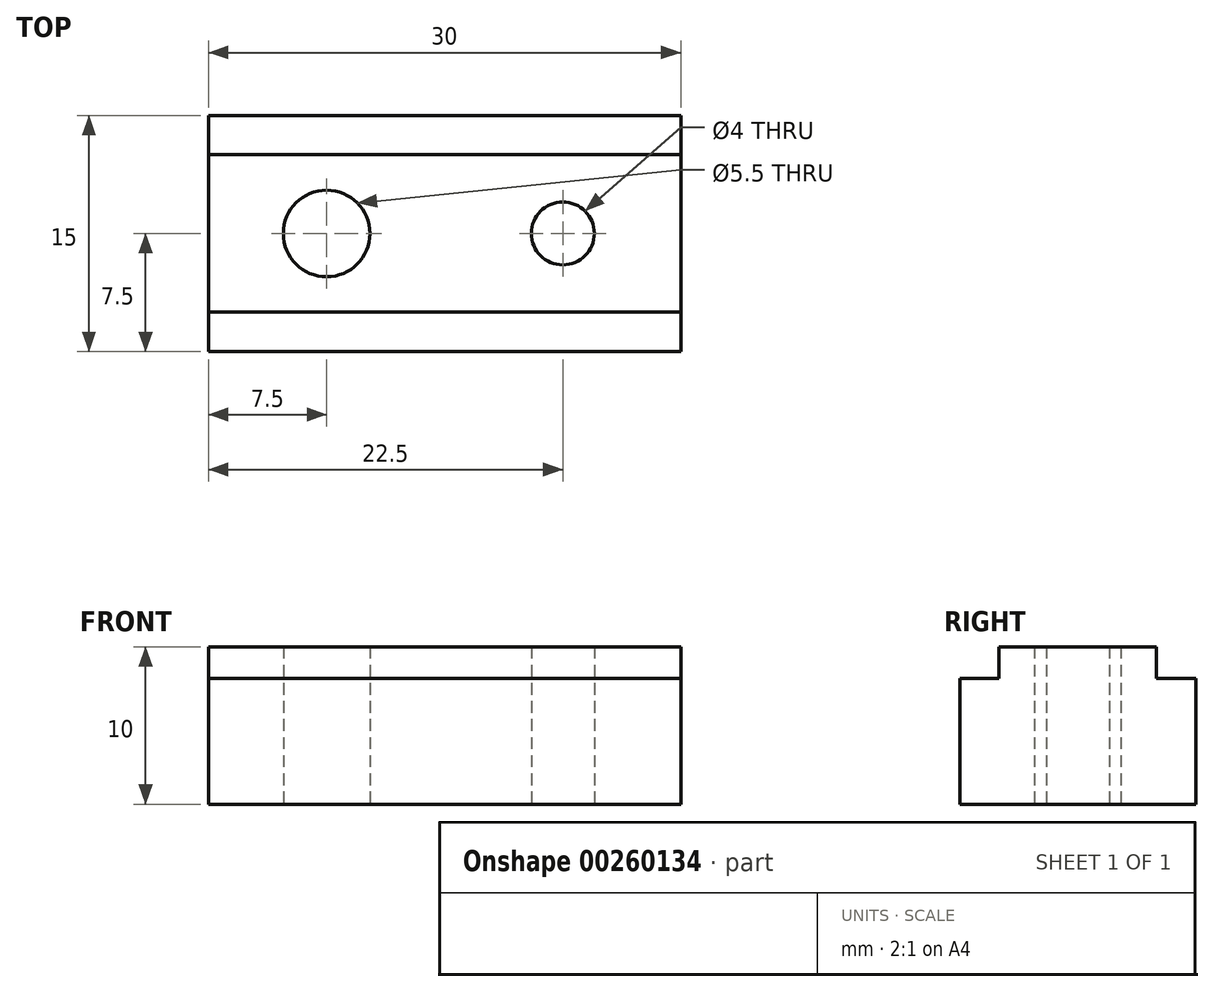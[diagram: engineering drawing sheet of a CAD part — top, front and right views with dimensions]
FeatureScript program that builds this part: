
annotation { "Feature Type Name" : "Feature", "Feature Type Description" : "" }
export const myFeature = defineFeature(function(context is Context, id is Id, definition is map)
    precondition{}
    {
        {
            var Q0;
            Q0=qCreatedBy(makeId("Top.planeOp"),FACE);
            var sketch = newSketch(context, id + "F0", { "sketchPlane" : qUnion([Q0])});
            skLineSegment(sketch, "E0.bottom", {"start": v(-15, -7.5) * mm, "end": v(15, -7.5) * mm});
            skLineSegment(sketch, "E0.top", {"start": v(-15, 7.5) * mm, "end": v(15, 7.5) * mm});
            skLineSegment(sketch, "E0.left", {"start": v(-15, -7.5) * mm, "end": v(-15, 7.5) * mm});
            skLineSegment(sketch, "E0.right", {"start": v(15, -7.5) * mm, "end": v(15, 7.5) * mm});
            skPoint(sketch, "E0.middle", {"position": v(0, 0) * mm});
            skLineSegment(sketch, "E1.bottom", {"start": v(-15, -5) * mm, "end": v(15, -5) * mm});
            skLineSegment(sketch, "E1.top", {"start": v(-15, 5) * mm, "end": v(15, 5) * mm});
            skLineSegment(sketch, "E1.left", {"start": v(-15, -5) * mm, "end": v(-15, 5) * mm});
            skLineSegment(sketch, "E1.right", {"start": v(15, -5) * mm, "end": v(15, 5) * mm});
            skSolve(sketch);
        }
        {
            var Q0;
            Q0=makeQuery(id+"F0.imprint","IMPRINT",FACE,{"disambiguationData":[TD([[makeQuery(id+"F0.imprint","IMPRINT",EDGE,{"derivedFrom":sQuery(id+"F0.wireOp",EDGE,"E1.bottom")}),1.0]])]});
            extrude(context, id + "F1", {"entities" : qUnion([Q0]), "depth" : 2 * mm});
        }
        {
            var Q0;
            Q0 = qSketchRegion(id + "F0", true);
            extrude(context, id + "F2", {"entities" : qUnion([Q0]), "operationType" : NewBodyOperationType.ADD, "oppositeDirection" : true, "depth" : 8 * mm});
        }
        {
            var Q0;
            Q0=qCreatedBy(makeId("Top.planeOp"),FACE);
            var sketch = newSketch(context, id + "F3", { "sketchPlane" : qUnion([Q0])});
            skLineSegment(sketch, "E2", {"start": v(0, 0) * mm, "end": v(0, 10) * mm, "construction": true});
            skLineSegment(sketch, "E3", {"start": v(0, 10) * mm, "end": v(-7.5, 10) * mm, "construction": true});
            skLineSegment(sketch, "E4", {"start": v(-7.5, 10) * mm, "end": v(-7.5, 0) * mm, "construction": true});
            skCircle(sketch, "E5", {"center": v(-7.5, 0) * mm, "radius": 2.75 * mm});
            skLineSegment(sketch, "E6", {"start": v(0, 0) * mm, "end": v(7.5, 0) * mm, "construction": true});
            skCircle(sketch, "E7", {"center": v(7.5, 0) * mm, "radius": 2 * mm});
            skSolve(sketch);
        }
        {
            var Q0;
            Q0 = qSketchRegion(id + "F3", true);
            var Q1;
            Q1=sQuery(id+"F3.wireOp",EDGE,"E7");
            var Q2;
            Q2=sQuery(id+"F3.wireOp",EDGE,"E5");
            extrude(context, id + "F4", {"entities" : qUnion([Q0]), "operationType" : NewBodyOperationType.REMOVE, "surfaceEntities" : qUnion([Q1, Q2]), "depth" : 25 * mm, "hasSecondDirection" : true, "secondDirectionOppositeDirection" : true, "secondDirectionDepth" : 25 * mm});
        }
    });
